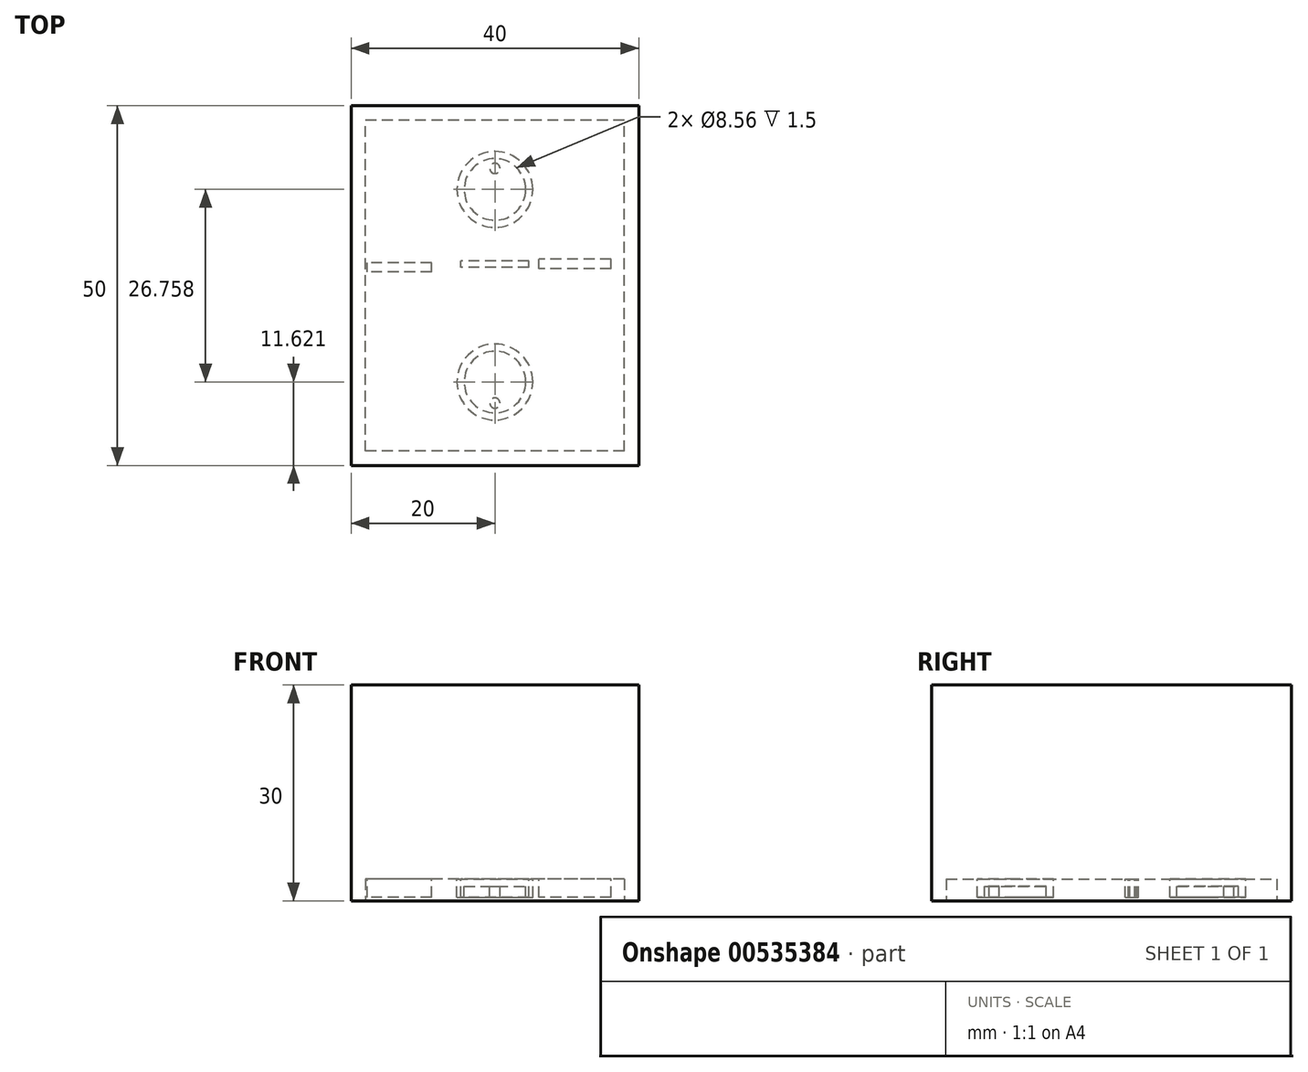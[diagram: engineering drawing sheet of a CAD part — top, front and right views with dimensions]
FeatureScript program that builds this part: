
annotation { "Feature Type Name" : "Feature", "Feature Type Description" : "" }
export const myFeature = defineFeature(function(context is Context, id is Id, definition is map)
    precondition{}
    {
        {
            var Q0;
            Q0=qCreatedBy(makeId("Front.planeOp"),FACE);
            var sketch = newSketch(context, id + "F0", { "sketchPlane" : qUnion([Q0])});
            skLineSegment(sketch, "E0.bottom", {"start": v(20, 15) * mm, "end": v(-20, 15) * mm});
            skLineSegment(sketch, "E0.top", {"start": v(20, -15) * mm, "end": v(-20, -15) * mm});
            skLineSegment(sketch, "E0.left", {"start": v(20, 15) * mm, "end": v(20, -15) * mm});
            skLineSegment(sketch, "E0.right", {"start": v(-20, 15) * mm, "end": v(-20, -15) * mm});
            skPoint(sketch, "E0.middle", {"position": v(0, 0) * mm});
            skSolve(sketch);
        }
        {
            var Q0;
            Q0 = qSketchRegion(id + "F0", true);
            var Q1;
            Q1=makeQuery(id+"F0.imprint","IMPRINT",FACE,{"disambiguationData":[TD([[makeQuery(id+"F0.imprint","IMPRINT",EDGE,{"derivedFrom":sQuery(id+"F0.wireOp",EDGE,"E0.bottom")}),1.0]])]});
            extrude(context, id + "F1", {"entities" : qUnion([Q0, Q1]), "depth" : 25 * mm, "offsetDistance" : 25 * mm, "hasSecondDirection" : true, "secondDirectionOppositeDirection" : true, "secondDirectionDepth" : 25 * mm});
        }
        {
            var Q0;
            Q0=makeQuery(id+"F1.opExtrude","SWEPT_FACE",FACE,{"disambiguationData":[OSD([sQuery(id+"F0.wireOp",EDGE,"E0.top")])]});
            shell(context, id + "F2", {"entities" : qUnion([Q0]), "thickness" : 2 * mm});
        }
        {
            var Q0;
            Q0=makeQuery(id+"F2.opShell","OFFSET_FACE",FACE,{"disambiguationData":[OSD([sQuery(id+"F0.wireOp",EDGE,"E0.bottom")])]});
            extrude(context, id + "F3", {"entities" : qUnion([Q0]), "operationType" : NewBodyOperationType.ADD, "depth" : 25 * mm, "offsetDistance" : 25 * mm});
        }
        {
            var Q0;
            Q0=makeQuery(id+"F3.opExtrude","CAP_FACE",FACE,{"disambiguationData":[OSD([sQuery(id+"F0.wireOp",EDGE,"E0.bottom")])],"isStart":false});
            var sketch = newSketch(context, id + "F4", { "sketchPlane" : qUnion([Q0])});
            skLineSegment(sketch, "E1.bottom", {"start": v(-8.8, -1.92) * mm, "end": v(-17.75, -1.92) * mm});
            skLineSegment(sketch, "E1.top", {"start": v(-8.8, -3.2) * mm, "end": v(-17.75, -3.2) * mm});
            skLineSegment(sketch, "E1.left", {"start": v(-8.8, -1.92) * mm, "end": v(-8.8, -3.2) * mm});
            skLineSegment(sketch, "E1.right", {"start": v(-17.75, -1.92) * mm, "end": v(-17.75, -3.2) * mm});
            skPoint(sketch, "E1.middle", {"position": v(-13.28, -2.56) * mm});
            skSolve(sketch);
        }
        {
            var Q0;
            Q0=makeQuery(id+"F4.imprint","IMPRINT",FACE,{"disambiguationData":[TD([[makeQuery(id+"F4.imprint","IMPRINT",EDGE,{"derivedFrom":sQuery(id+"F4.wireOp",EDGE,"E1.bottom")}),-1.0]])]});
            var sketch = newSketch(context, id + "F5", { "sketchPlane" : qUnion([Q0])});
            skLineSegment(sketch, "E2.bottom", {"start": v(4.73, -2.52) * mm, "end": v(-4.73, -2.52) * mm});
            skLineSegment(sketch, "E2.top", {"start": v(4.73, -3.47) * mm, "end": v(-4.73, -3.47) * mm});
            skLineSegment(sketch, "E2.left", {"start": v(4.73, -2.52) * mm, "end": v(4.73, -3.47) * mm});
            skLineSegment(sketch, "E2.right", {"start": v(-4.73, -2.52) * mm, "end": v(-4.73, -3.47) * mm});
            skPoint(sketch, "E2.middle", {"position": v(0, -3) * mm});
            skLineSegment(sketch, "E3.bottom", {"start": v(16.14, -2.35) * mm, "end": v(6.12, -2.35) * mm});
            skLineSegment(sketch, "E3.top", {"start": v(16.14, -3.72) * mm, "end": v(6.12, -3.72) * mm});
            skLineSegment(sketch, "E3.left", {"start": v(16.14, -2.35) * mm, "end": v(16.14, -3.72) * mm});
            skLineSegment(sketch, "E3.right", {"start": v(6.12, -2.35) * mm, "end": v(6.12, -3.72) * mm});
            skPoint(sketch, "E3.middle", {"position": v(11.13, -3.03) * mm});
            skSolve(sketch);
        }
        {
            var Q0;
            Q0 = qSketchRegion(id + "F5", true);
            var Q1;
            Q1=makeQuery(id+"F5.imprint","IMPRINT",FACE,{"disambiguationData":[TD([[makeQuery(id+"F5.imprint","IMPRINT",EDGE,{"derivedFrom":makeQuery(id+"F4.imprint","IMPRINT",EDGE,{"derivedFrom":sQuery(id+"F4.wireOp",EDGE,"E1.bottom")})}),1.0]])]});
            extrude(context, id + "F6", {"entities" : qUnion([Q0, Q1]), "operationType" : NewBodyOperationType.ADD, "depth" : 2.5 * mm, "offsetDistance" : 25 * mm});
        }
        {
            var Q0;
            Q0 = qSketchRegion(id + "F4", true);
            var sketch = newSketch(context, id + "F7", { "sketchPlane" : qUnion([Q0])});
            skCircle(sketch, "E4", {"center": v(0, -13.38) * mm, "radius": 5.28 * mm});
            skSolve(sketch);
        }
        {
            var Q0;
            Q0 = qSketchRegion(id + "F7", true);
            extrude(context, id + "F8", {"entities" : qUnion([Q0]), "depth" : 2.5 * mm, "offsetDistance" : 25 * mm});
        }
        {
            var Q0;
            Q0=makeQuery(id+"F8.opExtrude","CAP_FACE",FACE,{"disambiguationData":[OSD([sQuery(id+"F7.wireOp",EDGE,"E4")])],"isStart":false});
            shell(context, id + "F9", {"entities" : qUnion([Q0]), "thickness" : 1 * mm});
        }
        {
            var Q0;
            Q0=makeQuery(id+"F4.imprint","IMPRINT",FACE,{"disambiguationData":[TD([[makeQuery(id+"F4.imprint","IMPRINT",EDGE,{"derivedFrom":sQuery(id+"F4.wireOp",EDGE,"E1.bottom")}),-1.0]])]});
            var sketch = newSketch(context, id + "F10", { "sketchPlane" : qUnion([Q0])});
            skFitSpline(sketch, "E5", {"points": [v(-2.72, -13.47) * mm, v(-1.94, -12.16) * mm, v(0, -13.36) * mm, v(1.07, -12.1) * mm, v(2.48, -13.8) * mm], "startDerivative": vector(2.44, 9.22) * mm, "endDerivative": vector(5.66, -10.57) * mm});
            skFitSpline(sketch, "E6", {"points": [v(-1.92, -15.26) * mm, v(-1.11, -14.25) * mm, v(0, -15.22) * mm, v(1.24, -14.9) * mm, v(2.23, -14.99) * mm, v(3.31, -13.73) * mm], "startDerivative": vector(3.9, 8.12) * mm, "endDerivative": vector(4.65, 7.78) * mm});
            skSolve(sketch);
        }
        {
            var Q0;
            Q0=makeQuery(id+"F4.imprint","IMPRINT",FACE,{"disambiguationData":[TD([[makeQuery(id+"F4.imprint","IMPRINT",EDGE,{"derivedFrom":sQuery(id+"F4.wireOp",EDGE,"E1.bottom")}),-1.0]])]});
            var sketch = newSketch(context, id + "F11", { "sketchPlane" : qUnion([Q0])});
            skCircle(sketch, "E7", {"center": v(0, -16.3) * mm, "radius": 0.7 * mm});
            skSolve(sketch);
        }
        {
            var Q0;
            Q0 = qSketchRegion(id + "F11", true);
            var Q1;
            Q1 = qBodyType(qCreatedBy(id + "F10" ,EDGE), BodyType.WIRE);
            extrude(context, id + "F12", {"entities" : qUnion([Q0]), "bodyType" : ToolBodyType.SURFACE, "surfaceEntities" : qUnion([Q1]), "depth" : 2 * mm, "offsetDistance" : 25 * mm});
        }
        {
            var Q0;
            Q0 = qSketchRegion(id + "F11", true);
            extrude(context, id + "F13", {"entities" : qUnion([Q0]), "depth" : 2.5 * mm, "offsetDistance" : 25 * mm});
        }
        {
            var Q0;
            Q0=makeQuery(id+"F12.opExtrude","SWEPT_BODY",BODY,{"disambiguationData":[OSD([sQuery(id+"F10.wireOp",EDGE,"E5")])]});
            var Q1;
            Q1=makeQuery(id+"F12.opExtrude","SWEPT_BODY",BODY,{"disambiguationData":[OSD([sQuery(id+"F10.wireOp",EDGE,"E6")])]});
            var Q2;
            Q2=makeQuery(id+"F13.opExtrude","SWEPT_BODY",BODY,{"disambiguationData":[OSD([sQuery(id+"F11.wireOp",EDGE,"E7")])]});
            var Q3;
            Q3=makeQuery(id+"F8.opExtrude","SWEPT_BODY",BODY,{"disambiguationData":[OSD([sQuery(id+"F7.wireOp",EDGE,"E4")])]});
            var Q4;
            Q4=qCreatedBy(makeId("Front.planeOp"),FACE);
            mirror(context, id + "F14", {"operationType" : NewBodyOperationType.ADD, "entities" : qUnion([Q0, Q1, Q2, Q3]), "mirrorPlane" : qUnion([Q4])});
        }
    });
